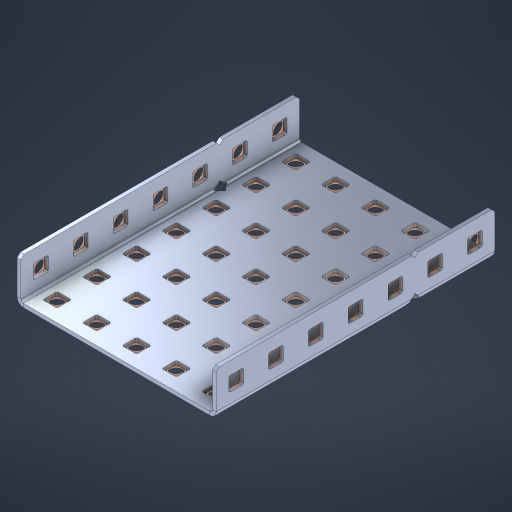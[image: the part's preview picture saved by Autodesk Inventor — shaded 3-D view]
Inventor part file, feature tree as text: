
AUTODESK INVENTOR PART (.ipt)
format: ipt  version: 2023 (Build 270158000, 158)  size: 848,384 bytes
history: native  units: in
note: dims shown in document units (in); Inventor stores cm internally (conversion verified against a paired STEP export)
features: other x54, extrude x48, sheet_metal_op x10, sketch x8, mirror x1, pattern_linear x1, chamfer x1
ambient origin geometry x8: Origin, YZ Plane, XZ Plane, XY Plane, X Axis, Y Axis, Z Axis, Center Point
bodies: Solid1 (feature_tree), Body (feature_tree)
feature tree (123):
  other  "Flange Pattern Plane"
  sheet_metal_op  "Flange Pattern"
  sheet_metal_op  "Body Pattern"
  other  "Arc Length"
  mirror  "Notch Mirror"
  pattern_linear  "Notch Pattern"  Spacing1=0.1875in  [1 undecoded]
  chamfer  "End Chamfer"
  extrude  "Half Cut"  Depth=0.0469in
  sketch  "Sketch1"  dims[d0=2.5in]
  other  "Plate1"
  sketch  "Sketch2"  dims[d1=3.5in]
  other  "Plate2"
  sheet_metal_op  "Bend1"
  sheet_metal_op  "Corner1"
  sketch  "Sketch3"  dims[d2=0.0469in]
  other  "Flange Pattern Sketch"
  sketch  "Sketch7"  dims[d3=0.0469in]
  other  "Srf1"
  other  "Srf2"
  sketch  "Sketch8"  dims[d4=0.0234in]
  sketch  "Sketch9"  dims[d5=0.0938in]
  other  "Srf91"
  sheet_metal_op  "Body Pattern Sketch"
  other  "Srf92"
  sketch  "Sketch13"  dims[d6=0.0469in]
  sketch  "Sketch14"  dims[d7=0.5in d8=90.0deg d9=0.0312in d10=0.1875in d11=0.0469in d12=0.0469in d16=0.182in d17=0.02in d18=0.0469in d19=0.0in d20=0.25in d21=0.25in d46=0.172in d47=1.0in d48=0.0in d49=0.182in d50=0.02in d51=0.25in d52=0.25in d53=0.0469in d54=0.0in d55=0.172in d56=1.0in d57=0.0in d60=2.7559in d62=0.5in d63=1.9685in d65=0.5in d85=0.1227in d86=0.1659in d88=0.04in d89=0.0469in d90=0.0in d91=0.04in d92=0.0491in d95=2.5in d96=0.04in d97=0.25in d98=45.0deg d101=0.0in d102=2.497in d131=2.5in d132=2.7559in d134=0.5in d139=0.5in]
  other  "Srf856"
  other  "Srf1310"
  other  "Srf1311"
  other  "Srf1312"
  other  "Srf1376"
  other  "Srf1377"
  other  "Srf1728"
  other  "Srf1755"
  other  "Srf1878"
  other  "Srf1879"
  other  "Srf1880"
  other  "Srf1881"
  other  "Srf1882"
  other  "Srf1883"
  other  "Srf1884"
  other  "Srf1885"
  other  "Srf1942"
  other  "Srf1943"
  other  "Srf1944"
  other  "Srf1945"
  other  "Srf1946"
  other  "Srf1947"
  other  "Srf1948"
  other  "Srf1949"
  other  "Srf1950"
  other  "Srf1951"
  other  "Srf1952"
  other  "Srf1953"
  other  "Srf1954"
  other  "Srf1955"
  other  "Srf1956"
  other  "Srf1957"
  other  "Srf1958"
  other  "Srf1959"
  other  "Srf1960"
  other  "Srf1961"
  other  "Srf1962"
  other  "Srf1963"
  other  "Srf1964"
  other  "Srf1965"
  other  "Srf1966"
  other  "Srf1967"
  other  "Srf1968"
  other  "Srf1969"
  other  "Srf1970"
  sheet_metal_op  "Flange Stamp"
  sheet_metal_op  "Flange Circle"
  sheet_metal_op  "Body Stamp"
  sheet_metal_op  "Body Circle"
  sheet_metal_op  "Notch"
  extrude  "ExtrusionSrf2"  Depth=0.0469in
  extrude  "ExtrusionSrf92"  Depth=2.5in
  extrude  "ExtrusionSrf856"  Depth=0.02in
  extrude  "ExtrusionSrf1310"  Depth=0.0469in
  extrude  "ExtrusionSrf1311"  TaperAngle=0.0deg  [1 undecoded]
  extrude  "ExtrusionSrf1312"  Depth=0.25in
  extrude  "ExtrusionSrf1376"  Depth=0.25in
  extrude  "ExtrusionSrf1377"  Depth=2.5in
  extrude  "ExtrusionSrf1728"  Depth=2.5in TaperAngle=0.0deg
  extrude  "ExtrusionSrf1755"  Depth=2.5in
  extrude  "ExtrusionSrf1878"  Depth=0.02in
  extrude  "ExtrusionSrf1879"  Depth=0.25in
  extrude  "ExtrusionSrf1880"  Depth=0.25in
  extrude  "ExtrusionSrf1881"  Depth=0.0469in
  extrude  "ExtrusionSrf1882"  TaperAngle=0.0deg  [1 undecoded]
  extrude  "ExtrusionSrf1883"  Depth=2.5in
  extrude  "ExtrusionSrf1884"  Depth=2.5in TaperAngle=0.0deg
  extrude  "ExtrusionSrf1885"  Depth=2.5in
  extrude  "ExtrusionSrf1942"  Depth=2.5in
  extrude  "ExtrusionSrf1943"  Depth=2.5in
  extrude  "ExtrusionSrf1944"  Depth=2.5in
  extrude  "ExtrusionSrf1945"  Depth=2.5in
  extrude  "ExtrusionSrf1946"  Depth=0.0469in
  extrude  "ExtrusionSrf1947"  TaperAngle=0.0deg  [1 undecoded]
  extrude  "ExtrusionSrf1948"  Depth=2.5in
  extrude  "ExtrusionSrf1949"  Depth=2.5in
  extrude  "ExtrusionSrf1950"  Depth=2.5in
  extrude  "ExtrusionSrf1951"  Depth=0.25in TaperAngle=45.0deg
  extrude  "ExtrusionSrf1952"  TaperAngle=0.0deg  [1 undecoded]
  extrude  "ExtrusionSrf1953"  Depth=2.5in
  extrude  "ExtrusionSrf1954"  Depth=2.5in
  extrude  "ExtrusionSrf1955"  Depth=2.5in
  extrude  "ExtrusionSrf1956"  Depth=2.5in
  extrude  "ExtrusionSrf1957"  Depth=2.5in
  extrude  "ExtrusionSrf1958"  [1 undecoded]
  extrude  "ExtrusionSrf1959"  [1 undecoded]
  extrude  "ExtrusionSrf1960"  [1 undecoded]
  extrude  "ExtrusionSrf1961"  [1 undecoded]
  extrude  "ExtrusionSrf1962"  [1 undecoded]
  extrude  "ExtrusionSrf1963"  [1 undecoded]
  extrude  "ExtrusionSrf1964"  [1 undecoded]
  extrude  "ExtrusionSrf1965"  [1 undecoded]
  extrude  "ExtrusionSrf1966"  [1 undecoded]
  extrude  "ExtrusionSrf1967"  [1 undecoded]
  extrude  "ExtrusionSrf1968"  [1 undecoded]
  extrude  "ExtrusionSrf1969"  [1 undecoded]
  extrude  "ExtrusionSrf1970"  [1 undecoded]
note: 18 required parameter values undecoded (feature->parameter linkage not recoverable at this tier; creation-order binding heuristic only, values carry confidence <= 0.55)
